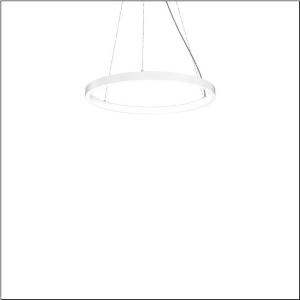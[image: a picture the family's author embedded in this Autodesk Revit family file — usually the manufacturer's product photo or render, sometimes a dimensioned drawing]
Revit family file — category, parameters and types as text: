
# Revit family: silica_r__21_ring-i_5pjbi2d1004a_0d30
name_source: partatom
category: Lighting Fixtures
units: mm (PartAtom-declared; Revit-internal decimal feet)

## family parameters
Cut with Voids When Loaded = No
Host = Face
Light Source = No
Part Type = Normal
Room Calculation Point = No
Round Connector Dimension = Use Diameter
Shared = No

## types (1)
- Silica® 21 Ring-I (1 x LED, 4800 lm, 80 W, 3000K)
    Apparent Load = 80 VA
    CIE Flux Codes = 22 48 76 50 101
    Color Rendering = 80
    Color Temperature = 3000K
    Default Elevation = 1800 mm
    Description = Silica® 21 Ring-I, suspended luminaire, of PMMA, frosted, light emission: inner ring side luminous distribution, primary light characteristic: symmetric, installation type: suspended mounting, LED, rated luminous flux: 4.800lm, luminous efficacy: 60lm/W, light colour: 830, colour temperature: 3000K, with terminal, 5-pole, mains connection: 230V, AC/DC, 0/50..60Hz, rated input power: 80W, housing, of extruded aluminium section, traffic white (RAL 9016), diameter: 805mm, ceiling canopy, traffic white (RAL 9016), protection rating (lamp compartment): IP40, insulation class (complete): insulation class I (protective earthing), certification: CE, impact resistance: IK02, permissible operating ambient temperature: 0..+35°C, packaging unit: 1 piece
    Height = 48 mm  [stored 0.15748 ft]
    Lamp = 1 x LED
    Lamp Light Flux = 4800 lm
    Lamp Power = 80 W
    Lamp count = 1
    Length = 805 mm
    Luminous efficacy = 60 lm/W
    Manufacturer = Siteco
    ModVariant = No
    Model = 5PJBI2D1004A
    Mounting Place = Ceiling
    Mounting Type = Pendant
    Number of Poles = 1
    OnlyDefault = Yes
    Power Factor = 1
    Product Name = Silica® 21 Ring-I
    Product group = suspended luminaire
    ProductGroupID = 904
    Protection Class = Protection class I
    Protection Degree = IP 40
    RLX_Detail_Level = 1
    RLX_Emergency_Light_Flux = 0 lm
    RLX_Emergency_Type = 0
    RLX_Emergency_Type_DB = No
    RlxData = <blob elided: 11553 chars, md5=fb8e8ee2>
    Socket = socket
    Standby Power = 0 W
    System Light Flux = 4800 lm
    System Power = 80 W
    Type Comments = Product without accessories
    Type Image = l_1258367.jpg
    URL = http://relux.com
    VarID = ---
    Voltage = 0 V
    Weight = 0.00 kg
    Width = 0 mm  [stored 0 ft]

note: [stored X ft] marks values corroborated as IEEE doubles in the binary element streams (Revit-internal decimal feet)

## geometry (parser evidence)
native form markers: Sweep x11
no freeform markers — native parametric forms only
